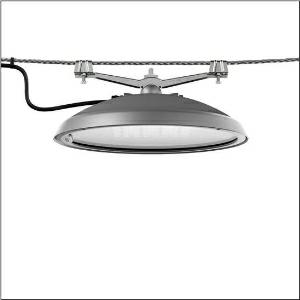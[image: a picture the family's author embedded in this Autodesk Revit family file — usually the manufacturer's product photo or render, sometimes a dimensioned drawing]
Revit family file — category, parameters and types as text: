
# Revit family: dl_50_iq_mini___st1_0s_5xa248w31f08re_ce8c
name_source: partatom
category: Lighting Fixtures
units: mm (PartAtom-declared; Revit-internal decimal feet)

## family parameters
Cut with Voids When Loaded = No
Host = Face
Light Source = No
Part Type = Normal
Room Calculation Point = No
Round Connector Dimension = Use Diameter
Shared = No

## types (1)
- --- (1 x LED, 6000 lm, 35.4 W, 3000K)
    Apparent Load = 35 VA
    CIE Flux Codes = 37 72 97 100 100
    Color Rendering = 70
    Color Temperature = 3000K
    Default Elevation = 1800 mm
    Description = DL 50 iQ mini, catenary luminaire, primary light control with lens, of PMMA, primary optical cover: cover, of toughened safety glass, transparent, light distribution: ST1.0s, light emission: direct distribution, primary light characteristic: symmetric, installation type: suspended mounting, LED, High Power LED, rated luminous flux: 6.000lm, luminous efficacy: 170lm/W, light colour: 730, colour temperature: 3000K, control gear: iQ Street-Remote, control: optimised constant luminous flux control (CLO 2.0), Desk-Remote (wireless, voltage-free reading and setting of iQ features in the workshop via application-optimized NFC function/RFID function), Light-Fading, Smart-Wire, Night-Set, Lumen-Switch, Temp-Guard, Auto-Match, Street-Remote, mains connection: 230..240V, AC, 50/60Hz, start of lifetime: 35W, end of service life: 36W, reduction: 17W, luminaire housing, of diecast aluminium, powder-coated, SITECO metallic grey (DB 702S), diameter: 500mm, height: 115mm, mounting height: 4..12m, protection rating (complete): IP66, insulation class (complete): insulation class II (safety insulation), certification: CE, ENEC, ENEC+, VDE, impact resistance: IK08, permissible operating ambient temperature for outdoor applications: -25..+40°C, standard-compliant lighting for roads and squares, packaging unit: 1 piece

Light Distribution: ST1.0s
    Height = 124 mm  [stored 0.406824 ft]
    Lamp = 1 x LED
    Lamp Light Flux = 6000 lm
    Lamp Power = 35.4 W
    Lamp count = 1
    Length = 500 mm
    Luminous efficacy = 169 lm/W
    Manufacturer = Siteco
    ModVariant = No
    Model = 5XA248W31F08RE
    Number of Poles = 1
    OnlyDefault = Yes
    Power Factor = 1
    Product Name = DL 50 iQ mini | ST1.0s
    Product group = catenary luminaire
    ProductGroupID = 6300
    Protection Class = Protection class II
    Protection Degree = IP 66
    RLX_Detail_Level = 1
    RLX_Emergency_Light_Flux = 0 lm
    RLX_Emergency_Type = 0
    RLX_Emergency_Type_DB = No
    RlxData = <blob elided: 123653 chars, md5=7a1b5069>
    Socket = socket
    Standby Power = 0 W
    System Light Flux = 6000 lm
    System Power = 35 W
    Type Comments = factory setting: luminous flux: 100 % | dim-lin: 254 | 376 mA
    Type Image = l_1242791.jpg
    URL = http://relux.com
    VarID = @adj_140249
    Voltage = 0 V
    Weight = 0.00 kg
    Width = 0 mm  [stored 0 ft]

note: [stored X ft] marks values corroborated as IEEE doubles in the binary element streams (Revit-internal decimal feet)

## geometry (parser evidence)
native form markers: Blend x4, Sweep x12
no freeform markers — native parametric forms only
